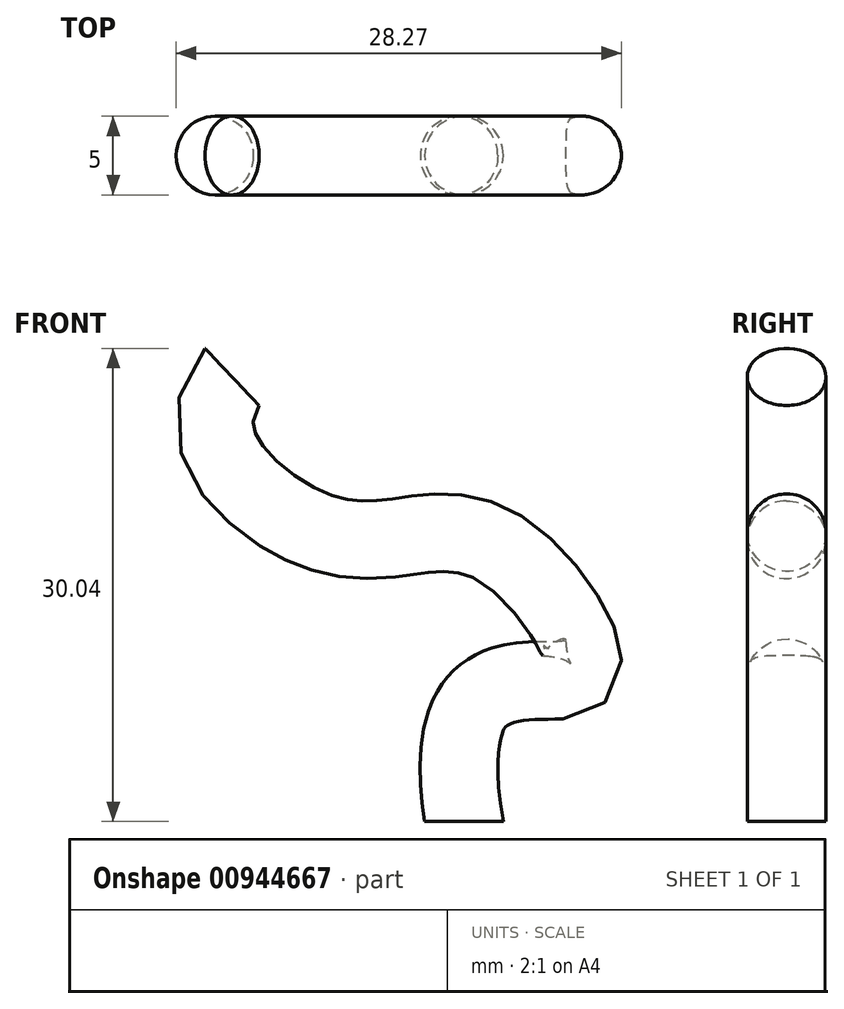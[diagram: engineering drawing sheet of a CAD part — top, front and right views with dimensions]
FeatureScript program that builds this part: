
annotation { "Feature Type Name" : "Feature", "Feature Type Description" : "" }
export const myFeature = defineFeature(function(context is Context, id is Id, definition is map)
    precondition{}
    {
        {
            var Q0;
            Q0=qCreatedBy(makeId("Top.planeOp"),FACE);
            var sketch = newSketch(context, id + "F0", { "sketchPlane" : qUnion([Q0])});
            skCircle(sketch, "E0", {"center": v(0, 0) * mm, "radius": 2.5 * mm});
            skSolve(sketch);
        }
        {
            var Q0;
            Q0=qCreatedBy(makeId("Front.planeOp"),FACE);
            var sketch = newSketch(context, id + "F1", { "sketchPlane" : qUnion([Q0])});
            skFitSpline(sketch, "E1", {"points": [v(0, 0) * mm, v(7.15, 9.29) * mm, v(2.51, 17.19) * mm, v(-4.56, 18) * mm, v(-10.93, 19.18) * mm, v(-14.73, 28.23) * mm], "startDerivative": vector(-24.95, 151.01) * mm, "endDerivative": vector(41.71, 54.95) * mm});
            skSolve(sketch);
        }
        {
            var Q0;
            Q0=makeQuery(id+"F0.imprint","IMPRINT",FACE,{"disambiguationData":[TD([[makeQuery(id+"F0.imprint","IMPRINT",EDGE,{"derivedFrom":sQuery(id+"F0.wireOp",EDGE,"E0")}),1.0]])]});
            var Q1;
            Q1=sQuery(id+"F1.wireOp",EDGE,"E1");
            sweep(context, id + "F2", {"profiles" : qUnion([Q0]), "path" : qUnion([Q1])});
        }
    });
